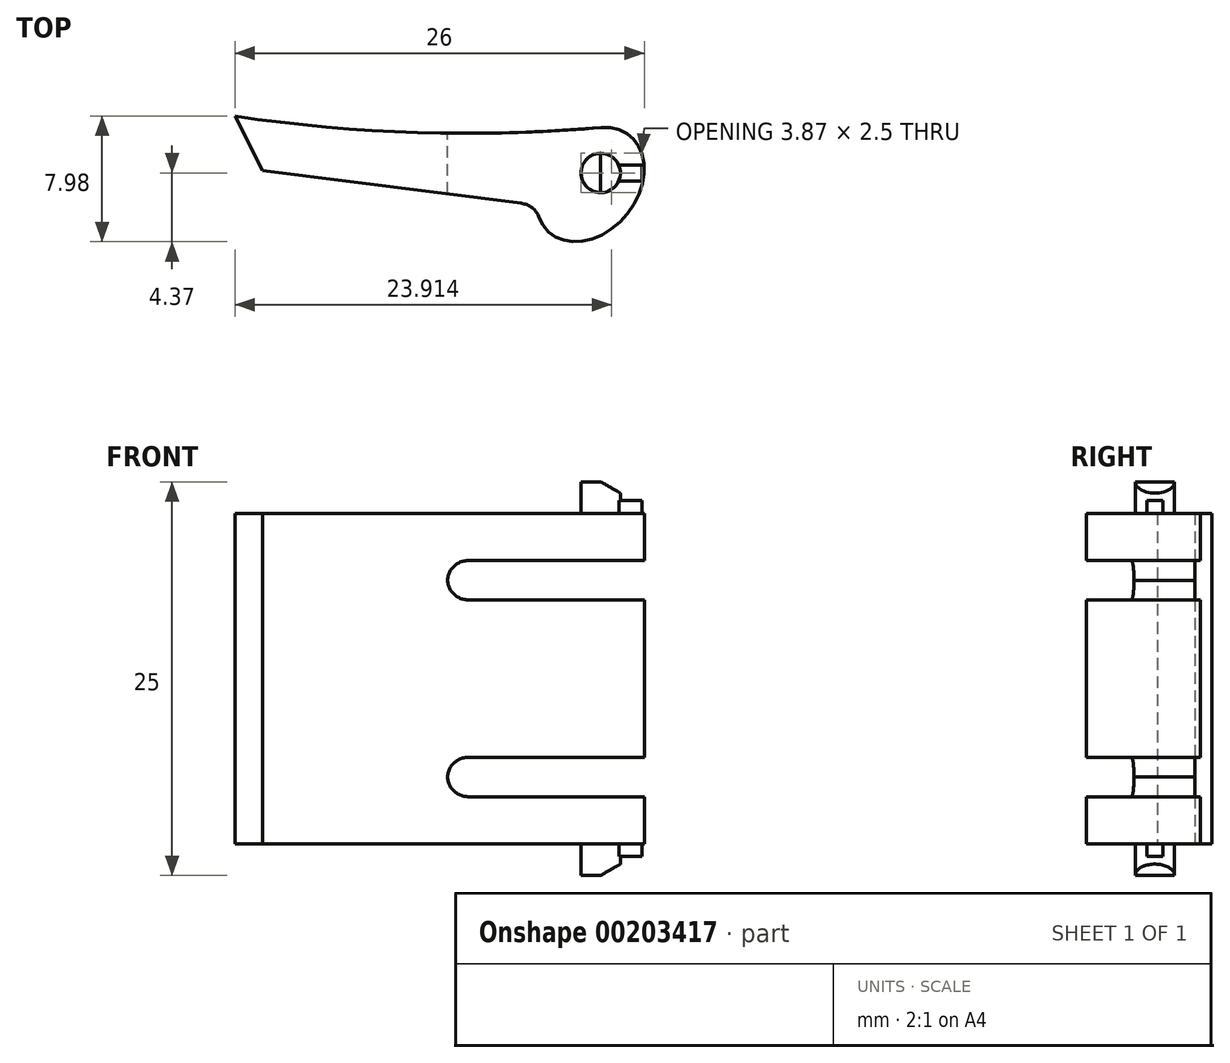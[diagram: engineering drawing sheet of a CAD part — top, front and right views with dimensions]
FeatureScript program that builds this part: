
annotation { "Feature Type Name" : "Feature", "Feature Type Description" : "" }
export const myFeature = defineFeature(function(context is Context, id is Id, definition is map)
    precondition{}
    {
        {
            var Q0;
            Q0=qCreatedBy(makeId("Top.planeOp"),FACE);
            var sketch = newSketch(context, id + "F0", { "sketchPlane" : qUnion([Q0])});
            skEllipticalArc(sketch, "E0", {});
            skArc(sketch, "E1", {"start": v(23.99, 33.57) * mm, "mid": v(35.59, 32.53) * mm, "end": v(47.23, 32.84) * mm});
            skLineSegment(sketch, "E2", {"start": v(23.99, 33.57) * mm, "end": v(25.75, 30.11) * mm});
            skLineSegment(sketch, "E3", {"start": v(25.75, 30.11) * mm, "end": v(43.13, 27.91) * mm});
            skLineSegment(sketch, "E4", {"start": v(49.99, 84.09) * mm, "end": v(49.99, -13.14) * mm, "construction": true});
            const initialGuessF0  = {"E0": [0.046550433067956865, 0.029223424269658058, 0.6332171771094439, 0.773974164049483, 0.004, 0.003, 2.490254055867803, 0.629940881996185]};
            skSetInitialGuess(sketch, initialGuessF0);
            skSolve(sketch);
        }
        {
            var Q0;
            Q0 = qSketchRegion(id + "F0", true);
            extrude(context, id + "F1", {"entities" : qUnion([Q0]), "depth" : 21 * mm});
        }
        {
            var Q0;
            Q0=makeQuery(id+"F1.opExtrude","CAP_FACE",FACE,{"disambiguationData":[OSD([sQuery(id+"F0.wireOp",EDGE,"E0"),sQuery(id+"F0.wireOp",EDGE,"E1"),sQuery(id+"F0.wireOp",EDGE,"E2"),sQuery(id+"F0.wireOp",EDGE,"E3")])],"isStart":false});
            cPlane(context, id + "F2", {"entities" : qUnion([Q0]), "cplaneType" : CPlaneType.OFFSET, "offset" : 3 * mm, "oppositeDirection" : true, "width" : 150 * mm, "height" : 150 * mm});
        }
        {
            var Q0;
            Q0=qCreatedBy(id+"F2.planeOp",FACE);
            var sketch = newSketch(context, id + "F3", { "sketchPlane" : qUnion([Q0])});
            skLineSegment(sketch, "E5.bottom", {"start": v(37.49, 16.76) * mm, "end": v(52.58, 16.76) * mm});
            skLineSegment(sketch, "E5.top", {"start": v(37.49, 41.92) * mm, "end": v(52.58, 41.92) * mm});
            skLineSegment(sketch, "E5.left", {"start": v(37.49, 16.76) * mm, "end": v(37.49, 41.92) * mm});
            skLineSegment(sketch, "E5.right", {"start": v(52.58, 16.76) * mm, "end": v(52.58, 41.92) * mm});
            skSolve(sketch);
        }
        {
            var Q0;
            Q0 = qSketchRegion(id + "F3", true);
            extrude(context, id + "F4", {"entities" : qUnion([Q0]), "operationType" : NewBodyOperationType.REMOVE, "oppositeDirection" : true, "depth" : 2.5 * mm});
        }
        {
            var Q0;
            Q0=makeQuery(id+"F1.opExtrude","CAP_FACE",FACE,{"disambiguationData":[OSD([sQuery(id+"F0.wireOp",EDGE,"E0"),sQuery(id+"F0.wireOp",EDGE,"E1"),sQuery(id+"F0.wireOp",EDGE,"E2"),sQuery(id+"F0.wireOp",EDGE,"E3")])],"isStart":true});
            cPlane(context, id + "F5", {"entities" : qUnion([Q0]), "cplaneType" : CPlaneType.OFFSET, "offset" : 3 * mm, "oppositeDirection" : true, "width" : 150 * mm, "height" : 150 * mm});
        }
        {
            var Q0;
            Q0=qCreatedBy(id+"F5.planeOp",FACE);
            var sketch = newSketch(context, id + "F6", { "sketchPlane" : qUnion([Q0])});
            skLineSegment(sketch, "E6.bottom", {"start": v(37.49, -18.3) * mm, "end": v(65.41, -18.3) * mm});
            skLineSegment(sketch, "E6.top", {"start": v(37.49, -40.67) * mm, "end": v(65.41, -40.67) * mm});
            skLineSegment(sketch, "E6.left", {"start": v(37.49, -18.3) * mm, "end": v(37.49, -40.67) * mm});
            skLineSegment(sketch, "E6.right", {"start": v(65.41, -18.3) * mm, "end": v(65.41, -40.67) * mm});
            skSolve(sketch);
        }
        {
            var Q0;
            Q0 = qSketchRegion(id + "F6", true);
            extrude(context, id + "F7", {"entities" : qUnion([Q0]), "operationType" : NewBodyOperationType.REMOVE, "oppositeDirection" : true, "depth" : 2.5 * mm});
        }
        {
            var Q0;
            Q0=makeQuery(id+"F7.boolean.opBoolean","COPY",EDGE,{"derivedFrom":makeQuery(id+"F7.opExtrude","CAP_EDGE",EDGE,{"disambiguationData":[OSD([sQuery(id+"F6.wireOp",EDGE,"E6.left")])],"isStart":false})});
            var Q1;
            Q1=makeQuery(id+"F4.boolean.opBoolean","COPY",EDGE,{"derivedFrom":makeQuery(id+"F4.opExtrude","CAP_EDGE",EDGE,{"disambiguationData":[OSD([sQuery(id+"F3.wireOp",EDGE,"E5.left")])],"isStart":true})});
            var Q2;
            Q2=makeQuery(id+"F7.boolean.opBoolean","COPY",EDGE,{"derivedFrom":makeQuery(id+"F7.opExtrude","CAP_EDGE",EDGE,{"disambiguationData":[OSD([sQuery(id+"F6.wireOp",EDGE,"E6.left")])],"isStart":true})});
            var Q3;
            Q3=makeQuery(id+"F4.boolean.opBoolean","COPY",EDGE,{"derivedFrom":makeQuery(id+"F4.opExtrude","CAP_EDGE",EDGE,{"disambiguationData":[OSD([sQuery(id+"F3.wireOp",EDGE,"E5.left")])],"isStart":false})});
            fillet(context, id + "F8", {"entities" : qUnion([Q0, Q1, Q2, Q3]), "radius" : 1.3 * mm, "allowEdgeOverflow" : false});
        }
        {
            var Q0;
            {var subQ0=sQuery(id+"F0.wireOp",EDGE,"E0");var subQ1=sQuery(id+"F0.wireOp",EDGE,"E3");Q0=makeQuery(id+"F4.boolean.opBoolean","SPLIT",EDGE,{"disambiguationData":[TD([makeQuery(id+"F1.opExtrude","CAP_FACE",FACE,{"disambiguationData":[OSD([subQ0,sQuery(id+"F0.wireOp",EDGE,"E1"),sQuery(id+"F0.wireOp",EDGE,"E2"),subQ1])],"isStart":false})])],"derivedFrom":makeQuery(id+"F1.opExtrude","SWEPT_EDGE",EDGE,{"disambiguationData":[OSD([subQ0,subQ1])]})});}
            var Q1;
            {var subQ0=sQuery(id+"F0.wireOp",EDGE,"E0");var subQ2=sQuery(id+"F0.wireOp",EDGE,"E3");var subQ4=makeQuery(id+"F4.opExtrude","CAP_FACE",FACE,{"disambiguationData":[OSD([sQuery(id+"F3.wireOp",EDGE,"E5.bottom"),sQuery(id+"F3.wireOp",EDGE,"E5.top"),sQuery(id+"F3.wireOp",EDGE,"E5.left"),sQuery(id+"F3.wireOp",EDGE,"E5.right")])],"isStart":false});Q1=makeQuery(id+"F7.boolean.opBoolean","SPLIT",EDGE,{"disambiguationData":[TD([makeQuery(id+"F4.boolean.opBoolean","COPY",FACE,{"derivedFrom":subQ4})])],"derivedFrom":makeQuery(id+"F4.boolean.opBoolean","SPLIT",EDGE,{"disambiguationData":[TD([makeQuery(id+"F1.opExtrude","CAP_FACE",FACE,{"disambiguationData":[OSD([subQ0,sQuery(id+"F0.wireOp",EDGE,"E1"),sQuery(id+"F0.wireOp",EDGE,"E2"),subQ2])],"isStart":true})])],"derivedFrom":makeQuery(id+"F1.opExtrude","SWEPT_EDGE",EDGE,{"disambiguationData":[OSD([subQ0,subQ2])]})})});}
            var Q2;
            {var subQ0=sQuery(id+"F0.wireOp",EDGE,"E0");var subQ2=sQuery(id+"F0.wireOp",EDGE,"E3");var subQ3=makeQuery(id+"F1.opExtrude","CAP_FACE",FACE,{"disambiguationData":[OSD([subQ0,sQuery(id+"F0.wireOp",EDGE,"E1"),sQuery(id+"F0.wireOp",EDGE,"E2"),subQ2])],"isStart":true});Q2=makeQuery(id+"F7.boolean.opBoolean","SPLIT",EDGE,{"disambiguationData":[TD([subQ3])],"derivedFrom":makeQuery(id+"F4.boolean.opBoolean","SPLIT",EDGE,{"disambiguationData":[TD([subQ3])],"derivedFrom":makeQuery(id+"F1.opExtrude","SWEPT_EDGE",EDGE,{"disambiguationData":[OSD([subQ0,subQ2])]})})});}
            fillet(context, id + "F9", {"entities" : qUnion([Q0, Q1, Q2]), "radius" : 1.4 * mm, "allowEdgeOverflow" : false});
        }
        {
            var Q0;
            Q0=makeQuery(id+"F1.opExtrude","CAP_FACE",FACE,{"disambiguationData":[OSD([sQuery(id+"F0.wireOp",EDGE,"E0"),sQuery(id+"F0.wireOp",EDGE,"E1"),sQuery(id+"F0.wireOp",EDGE,"E2"),sQuery(id+"F0.wireOp",EDGE,"E3")])],"isStart":false});
            var sketch = newSketch(context, id + "F10", { "sketchPlane" : qUnion([Q0])});
            skCircle(sketch, "E7", {"center": v(47.22, 29.96) * mm, "radius": 1.25 * mm});
            skSolve(sketch);
        }
        {
            var Q0;
            Q0 = qSketchRegion(id + "F10", true);
            extrude(context, id + "F11", {"entities" : qUnion([Q0]), "operationType" : NewBodyOperationType.ADD, "depth" : 2 * mm});
        }
        {
            var Q0;
            Q0=makeQuery(id+"F1.opExtrude","CAP_FACE",FACE,{"disambiguationData":[OSD([sQuery(id+"F0.wireOp",EDGE,"E0"),sQuery(id+"F0.wireOp",EDGE,"E1"),sQuery(id+"F0.wireOp",EDGE,"E2"),sQuery(id+"F0.wireOp",EDGE,"E3")])],"isStart":true});
            var sketch = newSketch(context, id + "F12", { "sketchPlane" : qUnion([Q0])});
            skSolve(sketch);
        }
        {
            var Q0;
            {var subQ2=sQuery(id+"F0.wireOp",EDGE,"E1");Q0=makeQuery(id+"F12.imprint","IMPRINT",FACE,{"disambiguationData":[TD([[makeQuery(id+"F12.imprint","IMPRINT",EDGE,{"derivedFrom":makeQuery(id+"F1.opExtrude","CAP_EDGE",EDGE,{"disambiguationData":[OSD([subQ2])],"isStart":true})}),1.0]])]});}
            var sketch = newSketch(context, id + "F13", { "sketchPlane" : qUnion([Q0])});
            skCircle(sketch, "E8.0", {"center": v(47.22, -29.96) * mm, "radius": 1.25 * mm});
            skSolve(sketch);
        }
        {
            var Q0;
            Q0 = qSketchRegion(id + "F13", true);
            extrude(context, id + "F14", {"entities" : qUnion([Q0]), "operationType" : NewBodyOperationType.ADD, "depth" : 2 * mm});
        }
        {
            var Q0;
            Q0=makeQuery(id+"F14.opExtrude","CAP_FACE",FACE,{"disambiguationData":[OSD([sQuery(id+"F13.wireOp",EDGE,"E8.0")])],"isStart":false});
            var sketch = newSketch(context, id + "F15", { "sketchPlane" : qUnion([Q0])});
            skCircle(sketch, "E9.0", {"center": v(47.22, -29.96) * mm, "radius": 1.25 * mm, "construction": true});
            skLineSegment(sketch, "E10", {"start": v(47.22, -28.7) * mm, "end": v(47.22, -31.2) * mm});
            skSolve(sketch);
        }
        {
            var Q0;
            Q0=sQuery(id+"F15.wireOp",EDGE,"E10");
            cPlane(context, id + "F16", {"entities" : qUnion([Q0]), "cplaneType" : CPlaneType.LINE_ANGLE, "offset" : 25 * mm, "angle" : 330 * degree, "width" : 150 * mm, "height" : 150 * mm});
        }
        {
            var Q0;
            Q0=qCreatedBy(id+"F16.planeOp",FACE);
            var sketch = newSketch(context, id + "F17", { "sketchPlane" : qUnion([Q0])});
            skLineSegment(sketch, "E11.bottom", {"start": v(39.88, 28.03) * mm, "end": v(41.38, 28.03) * mm});
            skLineSegment(sketch, "E11.top", {"start": v(39.88, 32.46) * mm, "end": v(41.38, 32.46) * mm});
            skLineSegment(sketch, "E11.left", {"start": v(39.88, 28.03) * mm, "end": v(39.88, 32.46) * mm});
            skLineSegment(sketch, "E11.right", {"start": v(41.38, 28.03) * mm, "end": v(41.38, 32.46) * mm});
            skSolve(sketch);
        }
        {
            var Q0;
            Q0 = qSketchRegion(id + "F17", true);
            extrude(context, id + "F18", {"entities" : qUnion([Q0]), "operationType" : NewBodyOperationType.REMOVE, "oppositeDirection" : true, "depth" : 25 * mm});
        }
        {
            var Q0;
            Q0=makeQuery(id+"F11.opExtrude","CAP_FACE",FACE,{"disambiguationData":[OSD([sQuery(id+"F10.wireOp",EDGE,"E7")])],"isStart":false});
            var sketch = newSketch(context, id + "F19", { "sketchPlane" : qUnion([Q0])});
            skCircle(sketch, "E12.0", {"center": v(47.22, 29.96) * mm, "radius": 1.25 * mm, "construction": true});
            skLineSegment(sketch, "E13", {"start": v(47.22, 31.2) * mm, "end": v(47.22, 28.7) * mm});
            skSolve(sketch);
        }
        {
            var Q0;
            Q0=sQuery(id+"F19.wireOp",EDGE,"E13");
            cPlane(context, id + "F20", {"entities" : qUnion([Q0]), "cplaneType" : CPlaneType.LINE_ANGLE, "offset" : 25 * mm, "angle" : 330 * degree, "width" : 150 * mm, "height" : 150 * mm});
        }
        {
            var Q0;
            Q0=qCreatedBy(id+"F20.planeOp",FACE);
            var sketch = newSketch(context, id + "F21", { "sketchPlane" : qUnion([Q0])});
            skLineSegment(sketch, "E14.bottom", {"start": v(29.4, -31.67) * mm, "end": v(31.3, -31.67) * mm});
            skLineSegment(sketch, "E14.top", {"start": v(29.4, -28.4) * mm, "end": v(31.3, -28.4) * mm});
            skLineSegment(sketch, "E14.left", {"start": v(29.4, -31.67) * mm, "end": v(29.4, -28.4) * mm});
            skLineSegment(sketch, "E14.right", {"start": v(31.3, -31.67) * mm, "end": v(31.3, -28.4) * mm});
            skLineSegment(sketch, "E15.0", {"start": v(29.4, -31.2) * mm, "end": v(29.4, -28.7) * mm, "construction": true});
            skSolve(sketch);
        }
        {
            var Q0;
            Q0 = qSketchRegion(id + "F21", true);
            extrude(context, id + "F22", {"entities" : qUnion([Q0]), "operationType" : NewBodyOperationType.REMOVE, "oppositeDirection" : true, "depth" : 25 * mm});
        }
        {
            var Q0;
            Q0=makeQuery(id+"F1.opExtrude","CAP_FACE",FACE,{"disambiguationData":[OSD([sQuery(id+"F0.wireOp",EDGE,"E0"),sQuery(id+"F0.wireOp",EDGE,"E1"),sQuery(id+"F0.wireOp",EDGE,"E2"),sQuery(id+"F0.wireOp",EDGE,"E3")])],"isStart":false});
            var sketch = newSketch(context, id + "F23", { "sketchPlane" : qUnion([Q0])});
            skCircle(sketch, "E16.0", {"center": v(47.22, 29.96) * mm, "radius": 1.25 * mm, "construction": true});
            skLineSegment(sketch, "E17.bottom", {"start": v(47.22, 30.46) * mm, "end": v(49.84, 30.46) * mm});
            skLineSegment(sketch, "E17.top", {"start": v(47.22, 29.46) * mm, "end": v(49.84, 29.46) * mm});
            skLineSegment(sketch, "E17.left", {"start": v(47.22, 30.46) * mm, "end": v(47.22, 29.46) * mm});
            skLineSegment(sketch, "E17.right", {"start": v(49.84, 30.46) * mm, "end": v(49.84, 29.46) * mm});
            skSolve(sketch);
        }
        {
            var Q0;
            Q0 = qSketchRegion(id + "F23", true);
            extrude(context, id + "F24", {"entities" : qUnion([Q0]), "operationType" : NewBodyOperationType.ADD, "depth" : 0.8 * mm});
        }
        {
            var Q0;
            {var subQ2=sQuery(id+"F0.wireOp",EDGE,"E1");Q0=makeQuery(id+"F12.imprint","IMPRINT",FACE,{"disambiguationData":[TD([[makeQuery(id+"F12.imprint","IMPRINT",EDGE,{"derivedFrom":makeQuery(id+"F1.opExtrude","CAP_EDGE",EDGE,{"disambiguationData":[OSD([subQ2])],"isStart":true})}),1.0]])]});}
            var sketch = newSketch(context, id + "F25", { "sketchPlane" : qUnion([Q0])});
            skLineSegment(sketch, "E18.0", {"start": v(47.22, -31.2) * mm, "end": v(47.22, -28.7) * mm, "construction": true});
            skLineSegment(sketch, "E19.bottom", {"start": v(47.22, -29.46) * mm, "end": v(49.85, -29.46) * mm});
            skLineSegment(sketch, "E19.top", {"start": v(47.22, -30.46) * mm, "end": v(49.85, -30.46) * mm});
            skLineSegment(sketch, "E19.left", {"start": v(47.22, -29.46) * mm, "end": v(47.22, -30.46) * mm});
            skLineSegment(sketch, "E19.right", {"start": v(49.85, -29.46) * mm, "end": v(49.85, -30.46) * mm});
            skSolve(sketch);
        }
        {
            var Q0;
            Q0 = qSketchRegion(id + "F25", true);
            extrude(context, id + "F26", {"entities" : qUnion([Q0]), "operationType" : NewBodyOperationType.ADD, "depth" : 0.8 * mm});
        }
    });
